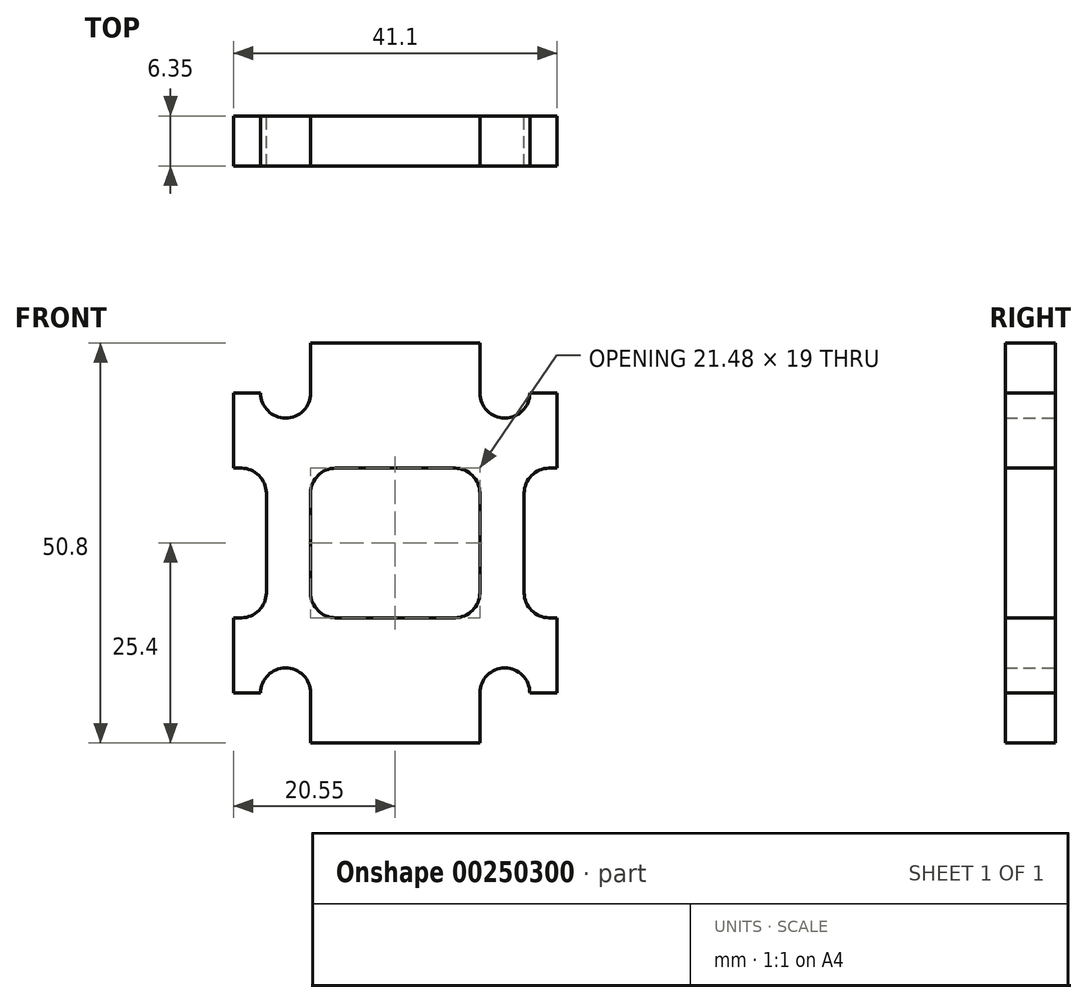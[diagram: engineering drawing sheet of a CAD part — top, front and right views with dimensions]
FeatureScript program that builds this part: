
annotation { "Feature Type Name" : "Feature", "Feature Type Description" : "" }
export const myFeature = defineFeature(function(context is Context, id is Id, definition is map)
    precondition{}
    {
        {
            var Q0;
            Q0=qCreatedBy(makeId("Front.planeOp"),FACE);
            var sketch = newSketch(context, id + "F0", { "sketchPlane" : qUnion([Q0])});
            skArc(sketch, "E0", {"start": v(17.1, -19.05) * mm, "mid": v(13.92, -15.88) * mm, "end": v(10.74, -19.05) * mm});
            skLineSegment(sketch, "E1", {"start": v(20.55, -19.05) * mm, "end": v(17.1, -19.05) * mm});
            skLineSegment(sketch, "E2", {"start": v(20.55, -9.5) * mm, "end": v(20.55, -19.05) * mm});
            skLineSegment(sketch, "E3", {"start": v(20.55, 19.05) * mm, "end": v(20.55, 9.5) * mm});
            skLineSegment(sketch, "E4", {"start": v(17.1, 19.05) * mm, "end": v(20.55, 19.05) * mm});
            skArc(sketch, "E5", {"start": v(10.74, 19.05) * mm, "mid": v(13.92, 15.87) * mm, "end": v(17.1, 19.05) * mm});
            skLineSegment(sketch, "E6", {"start": v(10.74, 25.4) * mm, "end": v(10.74, 19.05) * mm});
            skLineSegment(sketch, "E7", {"start": v(-10.74, 25.4) * mm, "end": v(10.74, 25.4) * mm});
            skLineSegment(sketch, "E8", {"start": v(-10.74, 19.05) * mm, "end": v(-10.74, 25.4) * mm});
            skArc(sketch, "E9", {"start": v(-17.1, 19.05) * mm, "mid": v(-13.92, 15.87) * mm, "end": v(-10.74, 19.05) * mm});
            skLineSegment(sketch, "E10", {"start": v(-20.55, 19.05) * mm, "end": v(-17.1, 19.05) * mm});
            skLineSegment(sketch, "E11", {"start": v(-20.55, 9.5) * mm, "end": v(-20.55, 19.05) * mm});
            skLineSegment(sketch, "E12", {"start": v(-20.55, -19.05) * mm, "end": v(-20.55, -9.5) * mm});
            skLineSegment(sketch, "E13", {"start": v(-17.1, -19.05) * mm, "end": v(-20.55, -19.05) * mm});
            skArc(sketch, "E14", {"start": v(-10.74, -19.05) * mm, "mid": v(-13.92, -15.88) * mm, "end": v(-17.1, -19.05) * mm});
            skLineSegment(sketch, "E15", {"start": v(-10.74, -25.4) * mm, "end": v(-10.74, -19.05) * mm});
            skLineSegment(sketch, "E16", {"start": v(10.74, -25.4) * mm, "end": v(-10.74, -25.4) * mm});
            skLineSegment(sketch, "E17", {"start": v(10.74, -19.05) * mm, "end": v(10.74, -25.4) * mm});
            skLineSegment(sketch, "E18", {"start": v(19.55, -9.5) * mm, "end": v(20.55, -9.5) * mm});
            skLineSegment(sketch, "E19", {"start": v(20.55, 9.5) * mm, "end": v(19.55, 9.5) * mm});
            skLineSegment(sketch, "E20", {"start": v(7.57, 9.5) * mm, "end": v(-7.57, 9.5) * mm});
            skLineSegment(sketch, "E21", {"start": v(-7.57, -9.5) * mm, "end": v(7.57, -9.5) * mm});
            skLineSegment(sketch, "E22", {"start": v(-19.55, -9.5) * mm, "end": v(-20.55, -9.5) * mm});
            skLineSegment(sketch, "E23", {"start": v(-20.55, 9.5) * mm, "end": v(-19.55, 9.5) * mm});
            skArc(sketch, "E24", {"start": v(16.38, -6.32) * mm, "mid": v(17.3, -8.57) * mm, "end": v(19.55, -9.5) * mm});
            skArc(sketch, "E25", {"start": v(19.55, 9.5) * mm, "mid": v(17.3, 8.57) * mm, "end": v(16.38, 6.32) * mm});
            skArc(sketch, "E26", {"start": v(-10.74, -6.32) * mm, "mid": v(-9.81, -8.57) * mm, "end": v(-7.57, -9.5) * mm});
            skArc(sketch, "E27", {"start": v(7.57, -9.5) * mm, "mid": v(9.81, -8.57) * mm, "end": v(10.74, -6.32) * mm});
            skArc(sketch, "E28", {"start": v(10.74, 6.32) * mm, "mid": v(9.81, 8.57) * mm, "end": v(7.57, 9.5) * mm});
            skArc(sketch, "E29", {"start": v(-7.57, 9.5) * mm, "mid": v(-9.81, 8.57) * mm, "end": v(-10.74, 6.32) * mm});
            skArc(sketch, "E30", {"start": v(-19.55, -9.5) * mm, "mid": v(-17.3, -8.57) * mm, "end": v(-16.38, -6.32) * mm});
            skArc(sketch, "E31", {"start": v(-16.38, 6.32) * mm, "mid": v(-17.3, 8.57) * mm, "end": v(-19.55, 9.5) * mm});
            skLineSegment(sketch, "E32", {"start": v(16.38, 6.32) * mm, "end": v(16.38, -6.32) * mm});
            skLineSegment(sketch, "E33", {"start": v(-16.38, 6.32) * mm, "end": v(-16.38, -6.32) * mm});
            skLineSegment(sketch, "E34", {"start": v(-10.74, 6.32) * mm, "end": v(-10.74, -6.32) * mm});
            skLineSegment(sketch, "E35", {"start": v(10.74, 6.32) * mm, "end": v(10.74, -6.32) * mm});
            skSolve(sketch);
        }
        {
            var Q0;
            Q0=makeQuery(id+"F0.imprint","IMPRINT",FACE,{"disambiguationData":[TD([[makeQuery(id+"F0.imprint","IMPRINT",EDGE,{"derivedFrom":sQuery(id+"F0.wireOp",EDGE,"E0")}),-1.0]])]});
            extrude(context, id + "F1", {"entities" : qUnion([Q0]), "depth" : 6.35 * mm});
        }
    });
